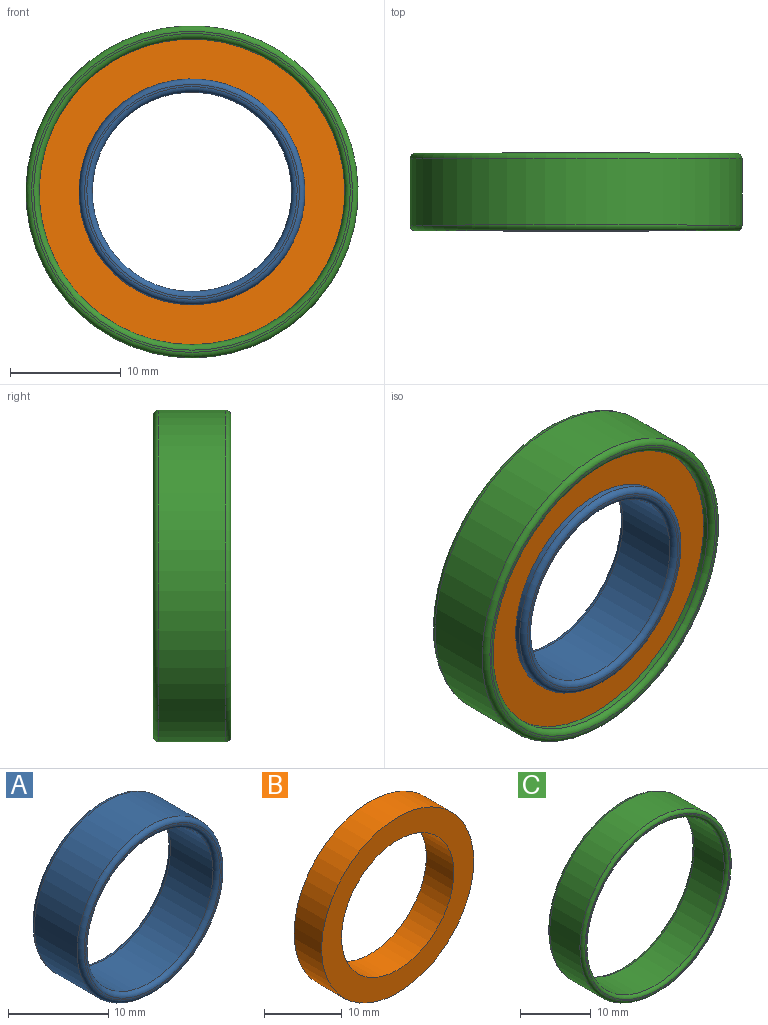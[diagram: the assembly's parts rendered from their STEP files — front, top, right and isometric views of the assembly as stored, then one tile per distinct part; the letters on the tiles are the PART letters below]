
ASSEMBLY  parts=3 mates=2
PART A: 8 faces, bbox 22.1x7x22.1 mm
  f0: cylinder r=9mm len=18mm, axis (0,1,0), area 339.3mm2, adj f4,f6
  f1: cylinder r=10.2mm len=20.4mm, axis (0,1,0), area 384.5mm2, adj f5,f7
  f2: plane 19.4x19.4mm, normal (0,-1,0), area 12.1mm2, adj f6,f7
  f3: plane 19.4x19.4mm, normal (0,1,0), area 12.1mm2, adj f4,f5
  f4: torus R=9.5mm, axis (0,-1,0), area 45.3mm2, adj f0,f3
  f5: torus R=9.7mm, axis (0,-1,0), area 49.4mm2, adj f1,f3
  f6: torus R=9.5mm, axis (0,-1,0), area 45.3mm2, adj f0,f2
  f7: torus R=9.7mm, axis (0,-1,0), area 49.4mm2, adj f1,f2
PART B: 4 faces, bbox 27.6x5x27.6 mm
  f0: cylinder r=10.2mm len=20.4mm, axis (0,1,0), area 320.4mm2, adj f2,f3
  f1: cylinder r=13.8mm len=27.6mm, axis (0,1,0), area 433.5mm2, adj f2,f3
  f2: plane 27.6x27.6mm, normal (0,-1,0), area 271.4mm2, adj f0,f1
  f3: plane 27.6x27.6mm, normal (0,1,0), area 271.4mm2, adj f0,f1
PART C: 8 faces, bbox 32.5x7x32.5 mm
  f0: cylinder r=13.8mm len=27.6mm, axis (0,1,0), area 520.2mm2, adj f5,f7
  f1: cylinder r=15mm len=30mm, axis (0,1,0), area 565.5mm2, adj f4,f6
  f2: plane 29x29mm, normal (0,-1,0), area 18.1mm2, adj f6,f7
  f3: plane 29x29mm, normal (0,1,0), area 18.1mm2, adj f4,f5
  f4: torus R=14.5mm, axis (0,-1,0), area 73.1mm2, adj f1,f3
  f5: torus R=14.3mm, axis (0,-1,0), area 69mm2, adj f0,f3
  f6: torus R=14.5mm, axis (0,-1,0), area 73.1mm2, adj f1,f2
  f7: torus R=14.3mm, axis (0,-1,0), area 69mm2, adj f0,f2
PLACE A at identity
PLACE B at identity
PLACE C at identity
MATE fastened B.f0 <-> C.f0  axis (0,1,0) through (0,0,0)mm
MATE fastened A.f0 <-> B.f0  axis (0,1,0) through (0,0,0)mm
